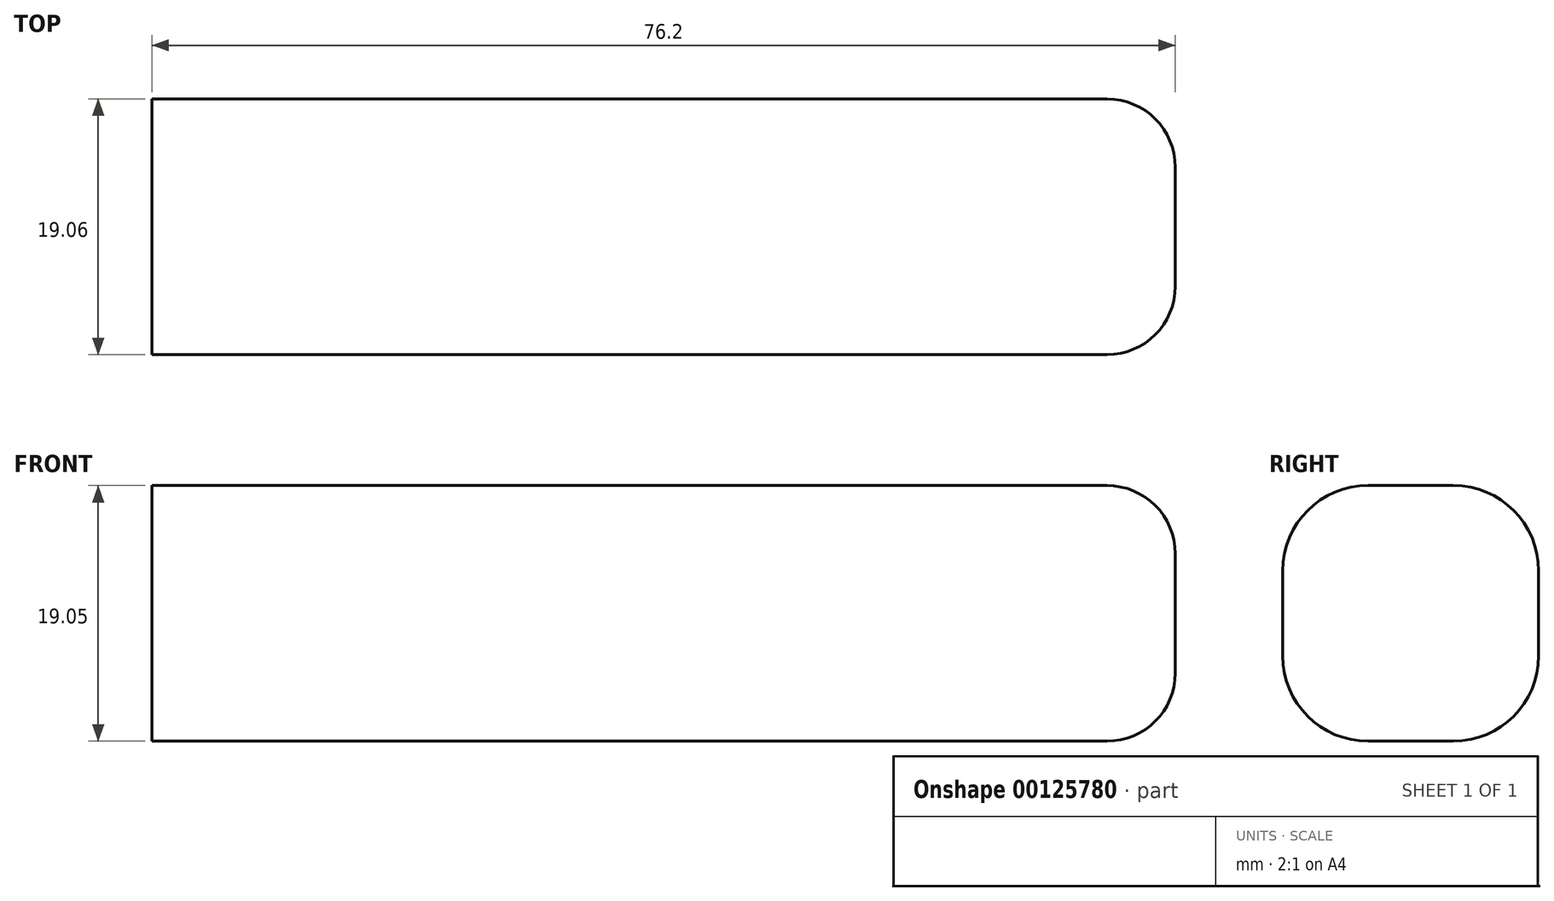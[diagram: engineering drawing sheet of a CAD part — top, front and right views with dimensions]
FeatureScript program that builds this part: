
annotation { "Feature Type Name" : "Feature", "Feature Type Description" : "" }
export const myFeature = defineFeature(function(context is Context, id is Id, definition is map)
    precondition{}
    {
        {
            var Q0;
            Q0=qCreatedBy(makeId("Front.planeOp"),FACE);
            var sketch = newSketch(context, id + "F0", { "sketchPlane" : qUnion([Q0])});
            skLineSegment(sketch, "E0.bottom", {"start": v(0, 11.69) * mm, "end": v(76.2, 11.69) * mm});
            skLineSegment(sketch, "E0.top", {"start": v(0, -7.36) * mm, "end": v(76.2, -7.36) * mm});
            skLineSegment(sketch, "E0.left", {"start": v(0, 11.69) * mm, "end": v(0, -7.36) * mm});
            skLineSegment(sketch, "E0.right", {"start": v(76.2, 11.69) * mm, "end": v(76.2, -7.36) * mm});
            skSolve(sketch);
        }
        {
            var Q0;
            Q0 = qSketchRegion(id + "F0", true);
            extrude(context, id + "F1", {"entities" : qUnion([Q0]), "endBound" : BoundingType.SYMMETRIC, "depth" : 19.05 * mm});
        }
        {
            var Q0;
            Q0=makeQuery(id+"F1.opExtrude","CAP_EDGE",EDGE,{"disambiguationData":[OSD([sQuery(id+"F0.wireOp",EDGE,"E0.bottom")])],"isStart":true});
            var Q1;
            Q1=makeQuery(id+"F1.opExtrude","CAP_EDGE",EDGE,{"disambiguationData":[OSD([sQuery(id+"F0.wireOp",EDGE,"E0.bottom")])],"isStart":false});
            var Q2;
            Q2=makeQuery(id+"F1.opExtrude","CAP_EDGE",EDGE,{"disambiguationData":[OSD([sQuery(id+"F0.wireOp",EDGE,"E0.top")])],"isStart":false});
            var Q3;
            Q3=makeQuery(id+"F1.opExtrude","CAP_EDGE",EDGE,{"disambiguationData":[OSD([sQuery(id+"F0.wireOp",EDGE,"E0.top")])],"isStart":true});
            fillet(context, id + "F2", {"entities" : qUnion([Q0, Q1, Q2, Q3]), "radius" : 6.35 * mm, "tangentPropagation" : true, "allowEdgeOverflow" : false});
        }
        {
            var Q0;
            Q0=makeQuery(id+"F1.opExtrude","SWEPT_EDGE",EDGE,{"disambiguationData":[OSD([sQuery(id+"F0.wireOp",EDGE,"E0.bottom"),sQuery(id+"F0.wireOp",EDGE,"E0.right")])]});
            fillet(context, id + "F3", {"entities" : qUnion([Q0]), "radius" : 5.08 * mm, "tangentPropagation" : true, "allowEdgeOverflow" : false});
        }
    });
